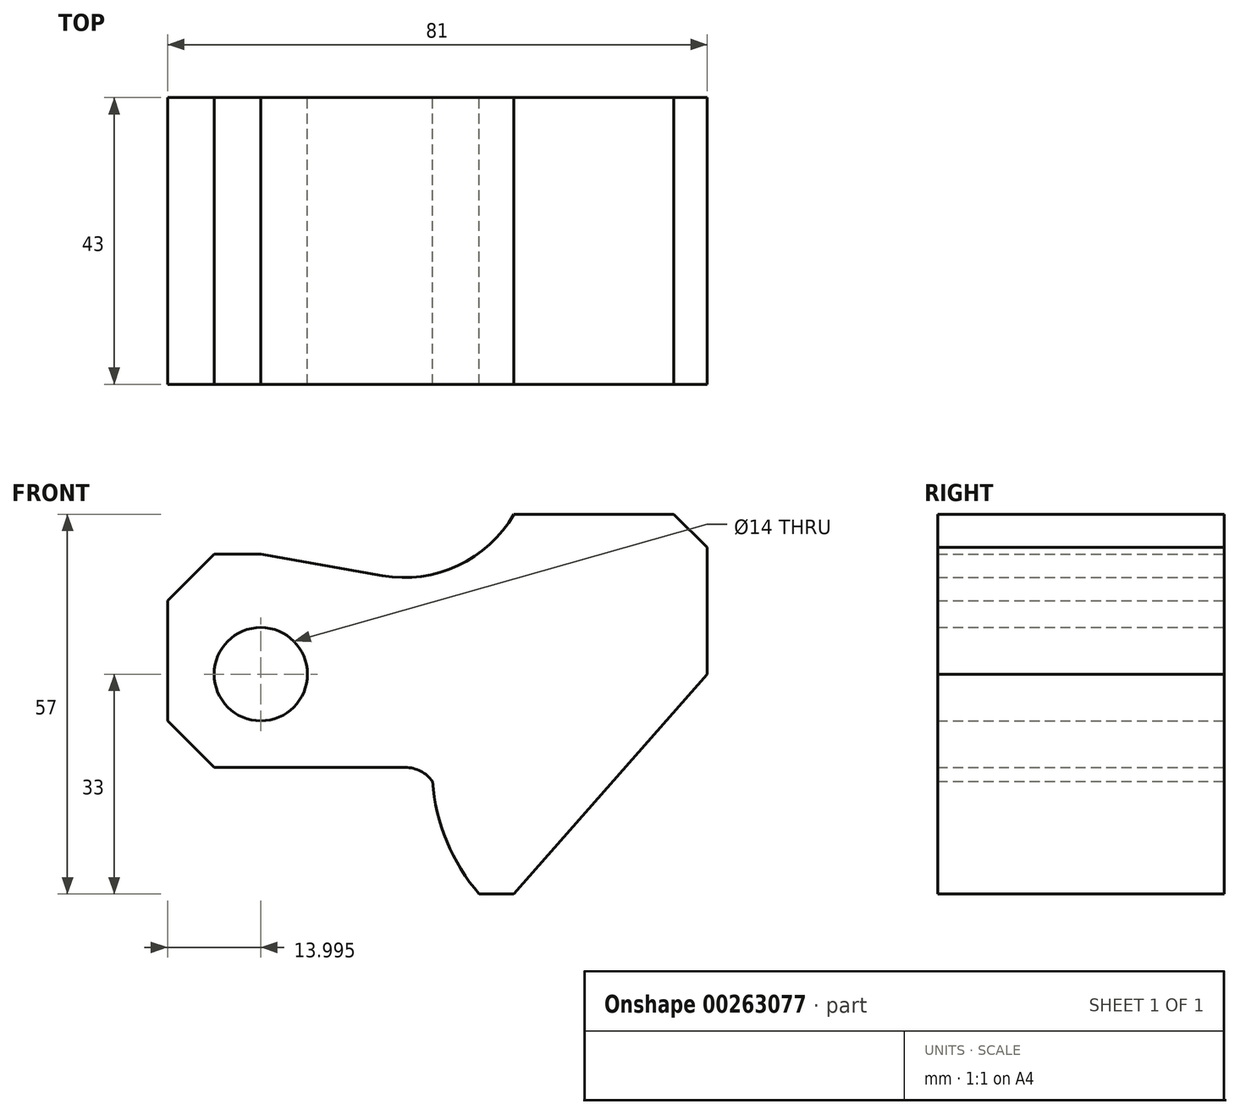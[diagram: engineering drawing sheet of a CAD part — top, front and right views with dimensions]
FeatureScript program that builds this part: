
annotation { "Feature Type Name" : "Feature", "Feature Type Description" : "" }
export const myFeature = defineFeature(function(context is Context, id is Id, definition is map)
    precondition{}
    {
        {
            var Q0;
            Q0=qCreatedBy(makeId("Front.planeOp"),FACE);
            var sketch = newSketch(context, id + "F0", { "sketchPlane" : qUnion([Q0])});
            skLineSegment(sketch, "E0", {"start": v(-13.08, -26) * mm, "end": v(-7.86, -26) * mm});
            skLineSegment(sketch, "E1", {"start": v(-7.86, -26) * mm, "end": v(21.14, 7) * mm});
            skLineSegment(sketch, "E2", {"start": v(21.14, 7) * mm, "end": v(21.14, 26) * mm});
            skLineSegment(sketch, "E3", {"start": v(21.14, 26) * mm, "end": v(16.14, 31) * mm});
            skLineSegment(sketch, "E4", {"start": v(16.14, 31) * mm, "end": v(-7.86, 31) * mm});
            skLineSegment(sketch, "E5", {"start": v(-52.86, 25) * mm, "end": v(-45.86, 25) * mm});
            skLineSegment(sketch, "E6", {"start": v(-52.86, 25) * mm, "end": v(-59.86, 18) * mm});
            skLineSegment(sketch, "E7", {"start": v(-59.86, 18) * mm, "end": v(-59.86, 0) * mm});
            skLineSegment(sketch, "E8", {"start": v(-59.86, 0) * mm, "end": v(-52.86, -7) * mm});
            skLineSegment(sketch, "E9", {"start": v(-52.86, -7) * mm, "end": v(-24.17, -7) * mm});
            skLineSegment(sketch, "E10", {"start": v(-45.86, 25) * mm, "end": v(-27.62, 21.78) * mm});
            skLineSegment(sketch, "E11", {"start": v(21.14, 26) * mm, "end": v(21.14, 67.07) * mm, "construction": true});
            skLineSegment(sketch, "E12", {"start": v(-45.86, 25) * mm, "end": v(-25.2, 25) * mm, "construction": true});
            skCircle(sketch, "E13", {"center": v(-45.86, 7) * mm, "radius": 7 * mm});
            skArc(sketch, "E14", {"start": v(-27.62, 21.78) * mm, "mid": v(-16.29, 23.28) * mm, "end": v(-7.86, 31) * mm});
            skArc(sketch, "E15", {"start": v(-20.1, -9.1) * mm, "mid": v(-17.95, -18.12) * mm, "end": v(-13.08, -26) * mm});
            skArc(sketch, "E16", {"start": v(-20.1, -9.1) * mm, "mid": v(-21.87, -7.56) * mm, "end": v(-24.17, -7) * mm});
            skSolve(sketch);
        }
        {
            var Q0;
            Q0=makeQuery(id+"F0.imprint","IMPRINT",FACE,{"disambiguationData":[TD([[makeQuery(id+"F0.imprint","IMPRINT",EDGE,{"derivedFrom":sQuery(id+"F0.wireOp",EDGE,"E0")}),1.0]])]});
            extrude(context, id + "F1", {"entities" : qUnion([Q0]), "depth" : 43 * mm});
        }
    });
